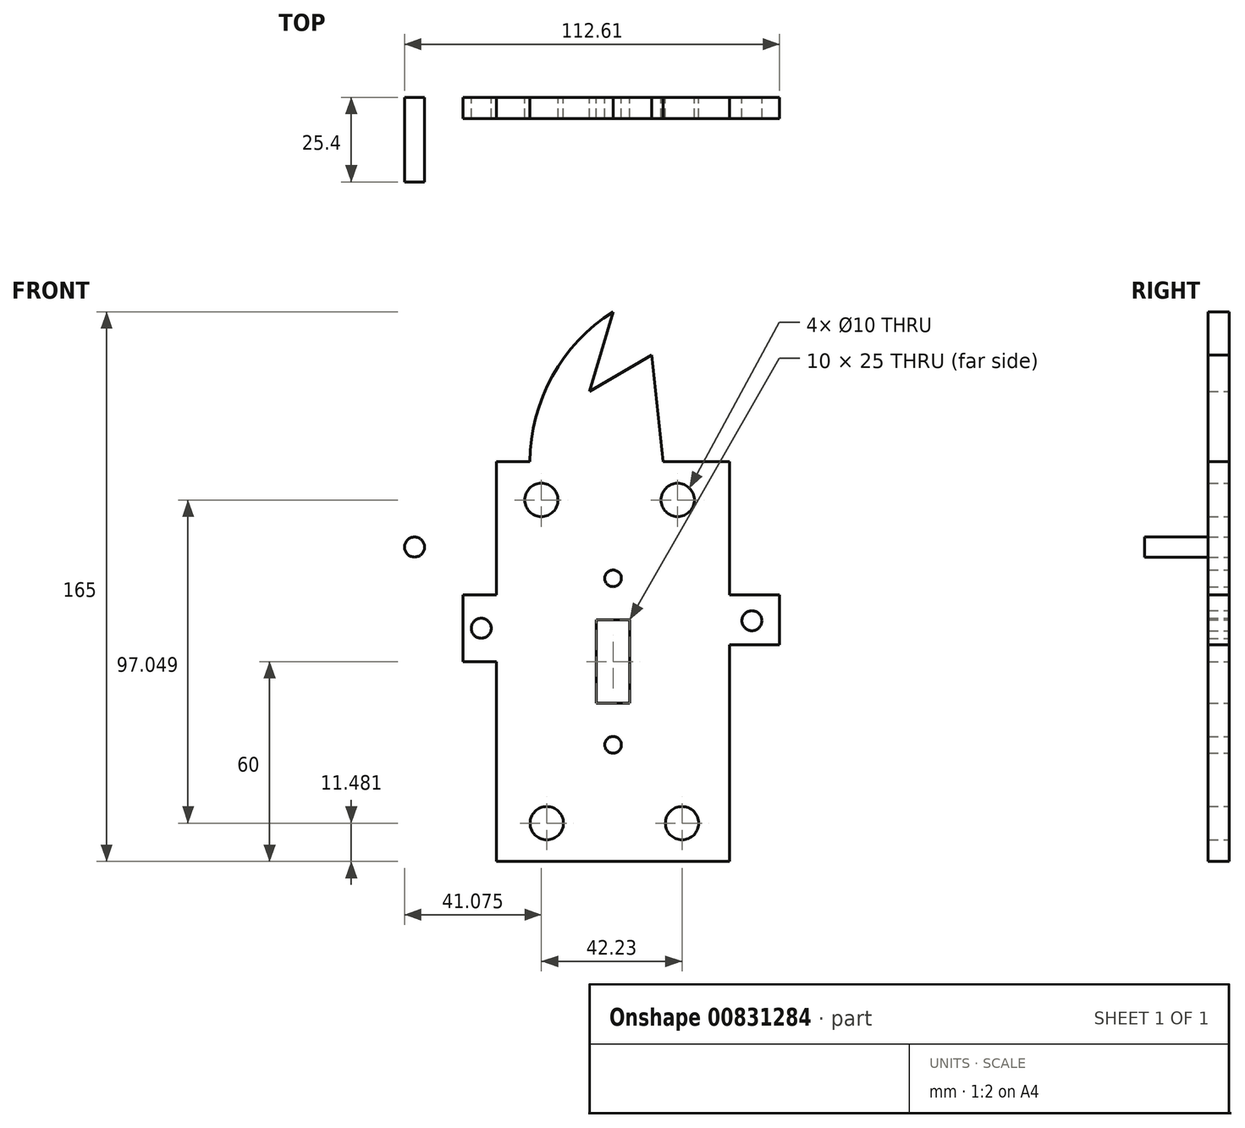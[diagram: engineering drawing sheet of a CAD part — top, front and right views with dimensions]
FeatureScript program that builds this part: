
annotation { "Feature Type Name" : "Feature", "Feature Type Description" : "" }
export const myFeature = defineFeature(function(context is Context, id is Id, definition is map)
    precondition{}
    {
        {
            var Q0;
            Q0=qCreatedBy(makeId("Front.planeOp"),FACE);
            var sketch = newSketch(context, id + "F0", { "sketchPlane" : qUnion([Q0])});
            skLineSegment(sketch, "E0.bottom", {"start": v(35, -60) * mm, "end": v(-35, -60) * mm});
            skLineSegment(sketch, "E0.top", {"start": v(35, 60) * mm, "end": v(-35, 60) * mm});
            skLineSegment(sketch, "E0.left", {"start": v(35, -60) * mm, "end": v(35, 60) * mm});
            skLineSegment(sketch, "E0.right", {"start": v(-35, -60) * mm, "end": v(-35, 60) * mm});
            skPoint(sketch, "E0.middle", {"position": v(0, 0) * mm});
            skPoint(sketch, "E1", {"position": v(-25, 60) * mm});
            skArc(sketch, "E2", {"start": v(0, 105) * mm, "mid": v(-18.24, 85.69) * mm, "end": v(-25, 60) * mm});
            skPoint(sketch, "E3", {"position": v(15, 60) * mm});
            skLineSegment(sketch, "E4", {"start": v(0, 105) * mm, "end": v(-7.06, 81.1) * mm});
            skLineSegment(sketch, "E5", {"start": v(-7.06, 81.1) * mm, "end": v(4.65, 87.98) * mm});
            skLineSegment(sketch, "E6", {"start": v(4.65, 87.98) * mm, "end": v(11.62, 92.07) * mm});
            skLineSegment(sketch, "E7", {"start": v(11.62, 92.07) * mm, "end": v(15, 60) * mm});
            skLineSegment(sketch, "E8.bottom", {"start": v(-5, -12.5) * mm, "end": v(5, -12.5) * mm});
            skLineSegment(sketch, "E8.top", {"start": v(-5, 12.5) * mm, "end": v(5, 12.5) * mm});
            skLineSegment(sketch, "E8.left", {"start": v(-5, -12.5) * mm, "end": v(-5, 12.5) * mm});
            skLineSegment(sketch, "E8.right", {"start": v(5, -12.5) * mm, "end": v(5, 12.5) * mm});
            skCircle(sketch, "E9", {"center": v(0, -25) * mm, "radius": 2.5 * mm});
            skCircle(sketch, "E10", {"center": v(0, 25) * mm, "radius": 2.5 * mm});
            skPoint(sketch, "E11", {"position": v(-35, 20) * mm});
            skLineSegment(sketch, "E12.bottom", {"start": v(-35, 20) * mm, "end": v(-45, 20) * mm});
            skLineSegment(sketch, "E12.top", {"start": v(-35, 0) * mm, "end": v(-45, 0) * mm});
            skLineSegment(sketch, "E12.left", {"start": v(-35, 20) * mm, "end": v(-35, 0) * mm});
            skLineSegment(sketch, "E12.right", {"start": v(-45, 20) * mm, "end": v(-45, 0) * mm});
            skPoint(sketch, "E13", {"position": v(35, 20) * mm});
            skLineSegment(sketch, "E14.bottom", {"start": v(35, 20) * mm, "end": v(50, 20) * mm});
            skLineSegment(sketch, "E14.top", {"start": v(35, 5) * mm, "end": v(50, 5) * mm});
            skLineSegment(sketch, "E14.left", {"start": v(35, 20) * mm, "end": v(35, 5) * mm});
            skLineSegment(sketch, "E14.right", {"start": v(50, 20) * mm, "end": v(50, 5) * mm});
            skCircle(sketch, "E15", {"center": v(41.68, 12.27) * mm, "radius": 3 * mm});
            skCircle(sketch, "E16", {"center": v(-39.57, 10) * mm, "radius": 3 * mm});
            skPoint(sketch, "E16.centerSnap0", {"position": v(-45, 10) * mm});
            skCircle(sketch, "E17", {"center": v(-59.61, 34.39) * mm, "radius": 3 * mm});
            skPoint(sketch, "E18", {"position": v(20.7, -48.52) * mm});
            skCircle(sketch, "E19", {"center": v(20.7, -48.52) * mm, "radius": 5 * mm});
            skCircle(sketch, "E20", {"center": v(-19.9, -48.52) * mm, "radius": 5 * mm});
            skCircle(sketch, "E21", {"center": v(19.39, 48.53) * mm, "radius": 5 * mm});
            skCircle(sketch, "E22", {"center": v(-21.54, 48.53) * mm, "radius": 5 * mm});
            skSolve(sketch);
        }
        {
            var Q0;
            {var subQ0=sQuery(id+"F0.wireOp",EDGE,"E2");Q0=makeQuery(id+"F0.imprint","IMPRINT",FACE,{"disambiguationData":[TD([[makeQuery(id+"F0.imprint","IMPRINT",EDGE,{"derivedFrom":subQ0}),1.0]])]});}
            var Q1;
            Q1=makeQuery(id+"F0.imprint","IMPRINT",FACE,{"disambiguationData":[TD([[makeQuery(id+"F0.imprint","IMPRINT",EDGE,{"derivedFrom":sQuery(id+"F0.wireOp",EDGE,"E0.bottom")}),-1.0]])]});
            var Q2;
            Q2=makeQuery(id+"F0.imprint","IMPRINT",FACE,{"disambiguationData":[TD([[makeQuery(id+"F0.imprint","IMPRINT",EDGE,{"derivedFrom":sQuery(id+"F0.wireOp",EDGE,"E12.bottom")}),1.0]])]});
            var Q3;
            Q3=makeQuery(id+"F0.imprint","IMPRINT",FACE,{"disambiguationData":[TD([[makeQuery(id+"F0.imprint","IMPRINT",EDGE,{"derivedFrom":sQuery(id+"F0.wireOp",EDGE,"E14.bottom")}),-1.0]])]});
            extrude(context, id + "F1", {"entities" : qUnion([Q0, Q1, Q2, Q3]), "depth" : 6.35 * mm, "offsetDistance" : 25.4 * mm});
        }
        {
            var Q0;
            Q0=makeQuery(id+"F0.imprint","IMPRINT",FACE,{"disambiguationData":[TD([[makeQuery(id+"F0.imprint","IMPRINT",EDGE,{"derivedFrom":sQuery(id+"F0.wireOp",EDGE,"E17")}),1.0]])]});
            extrude(context, id + "F2", {"entities" : qUnion([Q0]), "depth" : 25.4 * mm, "offsetDistance" : 25.4 * mm});
        }
    });
